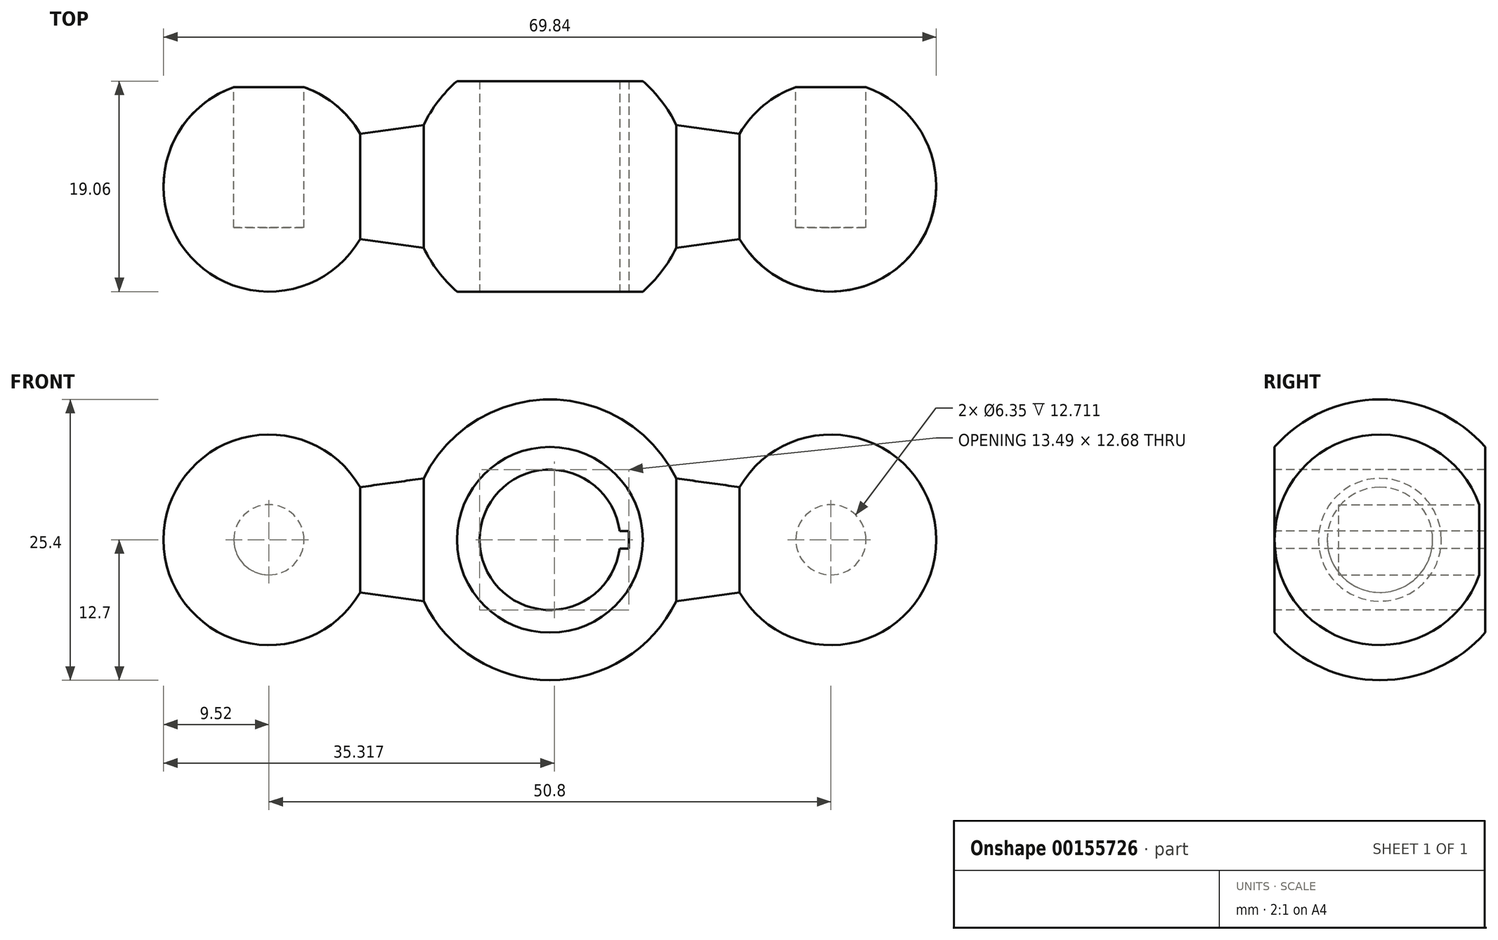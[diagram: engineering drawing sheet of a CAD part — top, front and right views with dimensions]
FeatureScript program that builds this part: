
annotation { "Feature Type Name" : "Feature", "Feature Type Description" : "" }
export const myFeature = defineFeature(function(context is Context, id is Id, definition is map)
    precondition{}
    {
        {
            var Q0;
            Q0=qCreatedBy(makeId("Top.planeOp"),FACE);
            var sketch = newSketch(context, id + "F0", { "sketchPlane" : qUnion([Q0])});
            skArc(sketch, "E0", {"start": v(11.42, 5.56) * mm, "mid": v(0, 12.7) * mm, "end": v(-11.42, 5.56) * mm});
            skLineSegment(sketch, "E1", {"start": v(-11.42, 5.56) * mm, "end": v(-17.15, 4.76) * mm});
            skLineSegment(sketch, "E2", {"start": v(11.42, 5.56) * mm, "end": v(17.15, 4.76) * mm});
            skLineSegment(sketch, "E3", {"start": v(-34.92, 0) * mm, "end": v(34.93, 0) * mm});
            skArc(sketch, "E4.converted", {"start": v(-17.15, 4.76) * mm, "mid": v(-27.87, 9.2) * mm, "end": v(-34.92, 0) * mm});
            skArc(sketch, "E5.converted", {"start": v(34.93, 0) * mm, "mid": v(27.87, 9.2) * mm, "end": v(17.15, 4.76) * mm});
            skPoint(sketch, "E6", {"position": v(25.4, 9.53) * mm});
            skSolve(sketch);
        }
        {
            var Q0;
            Q0 = qSketchRegion(id + "F0", true);
            var Q1;
            Q1=sQuery(id+"F0.wireOp",EDGE,"E3");
            revolve(context, id + "F7", {"entities" : qUnion([Q0]), "axis" : qUnion([Q1]), "revolveType" : RevolveType.FULL});
        }
        {
            var Q0;
            Q0=qCreatedBy(makeId("Top.planeOp"),FACE);
            var sketch = newSketch(context, id + "F8", { "sketchPlane" : qUnion([Q0])});
            skLineSegment(sketch, "E7.bottom", {"start": v(-8.4, 9.53) * mm, "end": v(8.4, 9.53) * mm});
            skLineSegment(sketch, "E7.top", {"start": v(-8.4, 12.7) * mm, "end": v(8.4, 12.7) * mm});
            skLineSegment(sketch, "E7.left", {"start": v(-8.4, 9.53) * mm, "end": v(-8.4, 12.7) * mm});
            skLineSegment(sketch, "E7.right", {"start": v(8.4, 9.53) * mm, "end": v(8.4, 12.7) * mm});
            skPoint(sketch, "E7.middle", {"position": v(0, 11.11) * mm});
            skLineSegment(sketch, "E8.bottom", {"start": v(-8.4, -12.7) * mm, "end": v(8.4, -12.7) * mm});
            skLineSegment(sketch, "E8.top", {"start": v(-8.4, -9.53) * mm, "end": v(8.4, -9.53) * mm});
            skLineSegment(sketch, "E8.left", {"start": v(-8.4, -12.7) * mm, "end": v(-8.4, -9.53) * mm});
            skLineSegment(sketch, "E8.right", {"start": v(8.4, -12.7) * mm, "end": v(8.4, -9.53) * mm});
            skPoint(sketch, "E8.middle", {"position": v(0, -11.11) * mm});
            skCircle(sketch, "E9", {"center": v(0, 0) * mm, "radius": 12.7 * mm, "construction": true});
            skSolve(sketch);
        }
        {
            var Q0;
            Q0 = qSketchRegion(id + "F8", true);
            extrude(context, id + "F1", {"entities" : qUnion([Q0]), "operationType" : NewBodyOperationType.REMOVE, "endBound" : BoundingType.THROUGH_ALL, "depth" : 25.4 * mm, "hasSecondDirection" : true, "secondDirectionBound" : SecondDirectionBoundingType.THROUGH_ALL, "secondDirectionOppositeDirection" : true, "secondDirectionDepth" : 25.4 * mm});
        }
        {
            var Q0;
            Q0=makeQuery(id+"F1.boolean.opBoolean","COPY",FACE,{"derivedFrom":makeQuery(id+"F1.opExtrude","SWEPT_FACE",FACE,{"disambiguationData":[OSD([sQuery(id+"F8.wireOp",EDGE,"E8.top")])]})});
            var sketch = newSketch(context, id + "F2", { "sketchPlane" : qUnion([Q0])});
            skCircle(sketch, "E10", {"center": v(0, 0) * mm, "radius": 6.35 * mm});
            skLineSegment(sketch, "E11.bottom", {"start": v(7.14, -0.8) * mm, "end": v(6.3, -0.8) * mm});
            skLineSegment(sketch, "E11.top", {"start": v(7.14, 0.8) * mm, "end": v(6.3, 0.8) * mm});
            skLineSegment(sketch, "E11.left", {"start": v(7.14, -0.8) * mm, "end": v(7.14, 0.8) * mm});
            skLineSegment(sketch, "E11.right", {"start": v(6.3, -0.8) * mm, "end": v(6.3, 0.8) * mm, "construction": true});
            skPoint(sketch, "E11.middle", {"position": v(6.72, 0) * mm});
            skSolve(sketch);
        }
        {
            var Q0;
            Q0 = qSketchRegion(id + "F2", true);
            extrude(context, id + "F3", {"entities" : qUnion([Q0]), "operationType" : NewBodyOperationType.REMOVE, "endBound" : BoundingType.UP_TO_NEXT, "oppositeDirection" : true, "depth" : 25.4 * mm});
        }
        {
            var Q0;
            Q0=qCreatedBy(makeId("Front.planeOp"),FACE);
            var Q1;
            Q1=sQuery(id+"F0.wireOp",VERTEX,"E6");
            cPlane(context, id + "F4", {"entities" : qUnion([Q0, Q1]), "cplaneType" : CPlaneType.PLANE_POINT, "offset" : 25.4 * mm, "width" : 152.4 * mm, "height" : 152.4 * mm});
        }
        {
            var Q0;
            Q0=qCreatedBy(id+"F4.planeOp",FACE);
            var sketch = newSketch(context, id + "F5", { "sketchPlane" : qUnion([Q0])});
            skCircle(sketch, "E12", {"center": v(25.4, 0) * mm, "radius": 3.18 * mm});
            skCircle(sketch, "E13", {"center": v(-25.4, 0) * mm, "radius": 3.18 * mm});
            skSolve(sketch);
        }
        {
            var Q0;
            Q0 = qSketchRegion(id + "F5", true);
            extrude(context, id + "F6", {"entities" : qUnion([Q0]), "operationType" : NewBodyOperationType.REMOVE, "depth" : 13.26 * mm});
        }
    });
